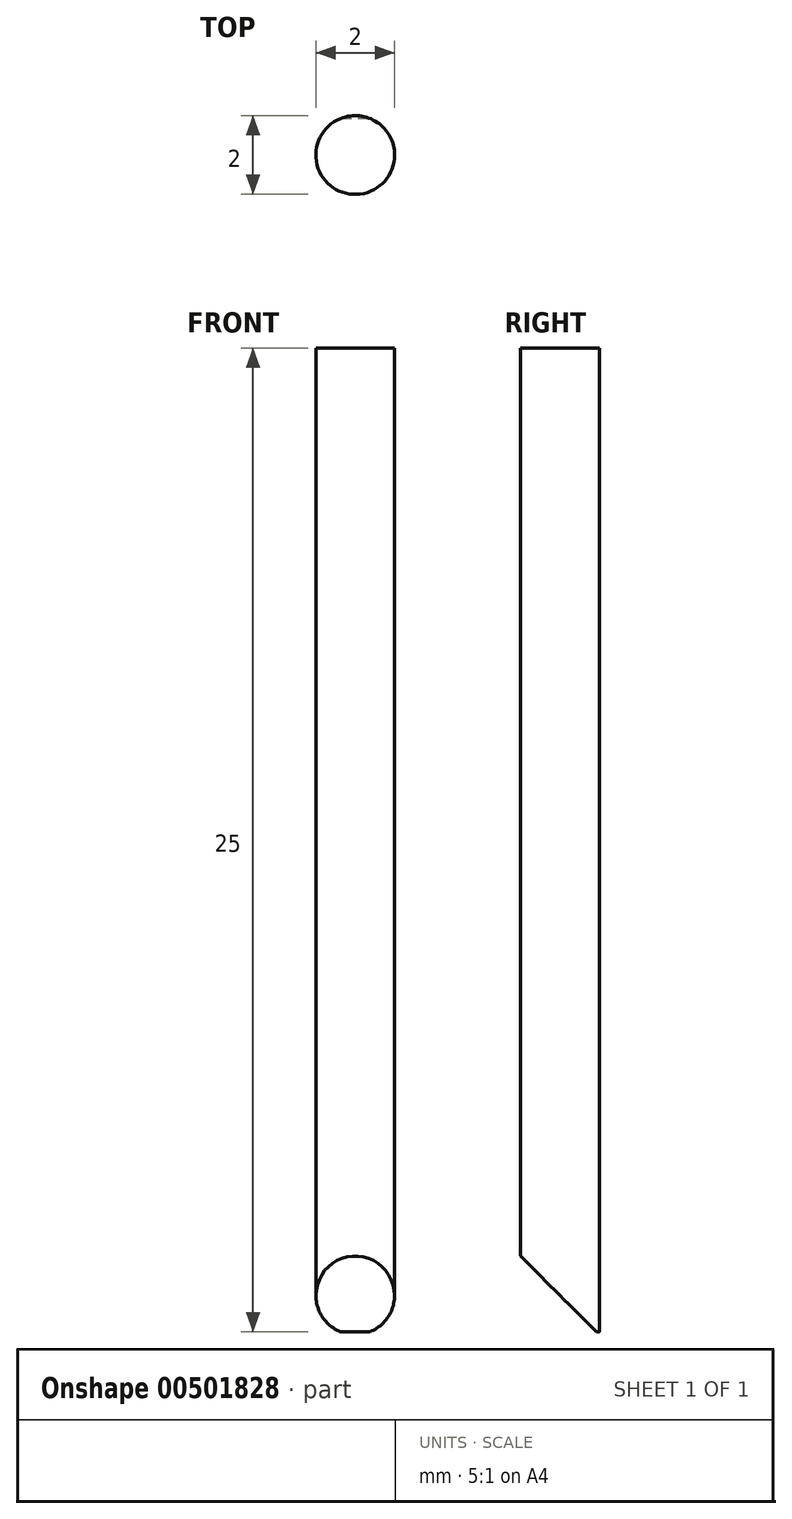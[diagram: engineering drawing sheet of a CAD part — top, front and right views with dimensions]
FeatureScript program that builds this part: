
annotation { "Feature Type Name" : "Feature", "Feature Type Description" : "" }
export const myFeature = defineFeature(function(context is Context, id is Id, definition is map)
    precondition{}
    {
        {
            var Q0;
            Q0=qCreatedBy(makeId("Top.planeOp"),FACE);
            var sketch = newSketch(context, id + "F0", { "sketchPlane" : qUnion([Q0])});
            skCircle(sketch, "E0", {"center": v(0, 0) * mm, "radius": 1 * mm});
            skSolve(sketch);
        }
        {
            var Q0;
            Q0 = qSketchRegion(id + "F0", true);
            extrude(context, id + "F1", {"entities" : qUnion([Q0]), "depth" : 25 * mm});
        }
        {
            var Q0;
            Q0=qCreatedBy(makeId("Right.planeOp"),FACE);
            var sketch = newSketch(context, id + "F2", { "sketchPlane" : qUnion([Q0])});
            skLineSegment(sketch, "E1", {"start": v(2.04, -1.1) * mm, "end": v(-1.4, 2.33) * mm});
            skLineSegment(sketch, "E2", {"start": v(-1.4, 2.33) * mm, "end": v(-1.4, -1.1) * mm});
            skLineSegment(sketch, "E3", {"start": v(-1.4, -1.1) * mm, "end": v(2.04, -1.1) * mm});
            skSolve(sketch);
        }
        {
            var Q0;
            Q0 = qSketchRegion(id + "F2", true);
            extrude(context, id + "F3", {"entities" : qUnion([Q0]), "operationType" : NewBodyOperationType.REMOVE, "oppositeDirection" : true, "depth" : 25 * mm, "hasSecondDirection" : true, "secondDirectionOppositeDirection" : false, "secondDirectionDepth" : 25 * mm});
        }
    });
